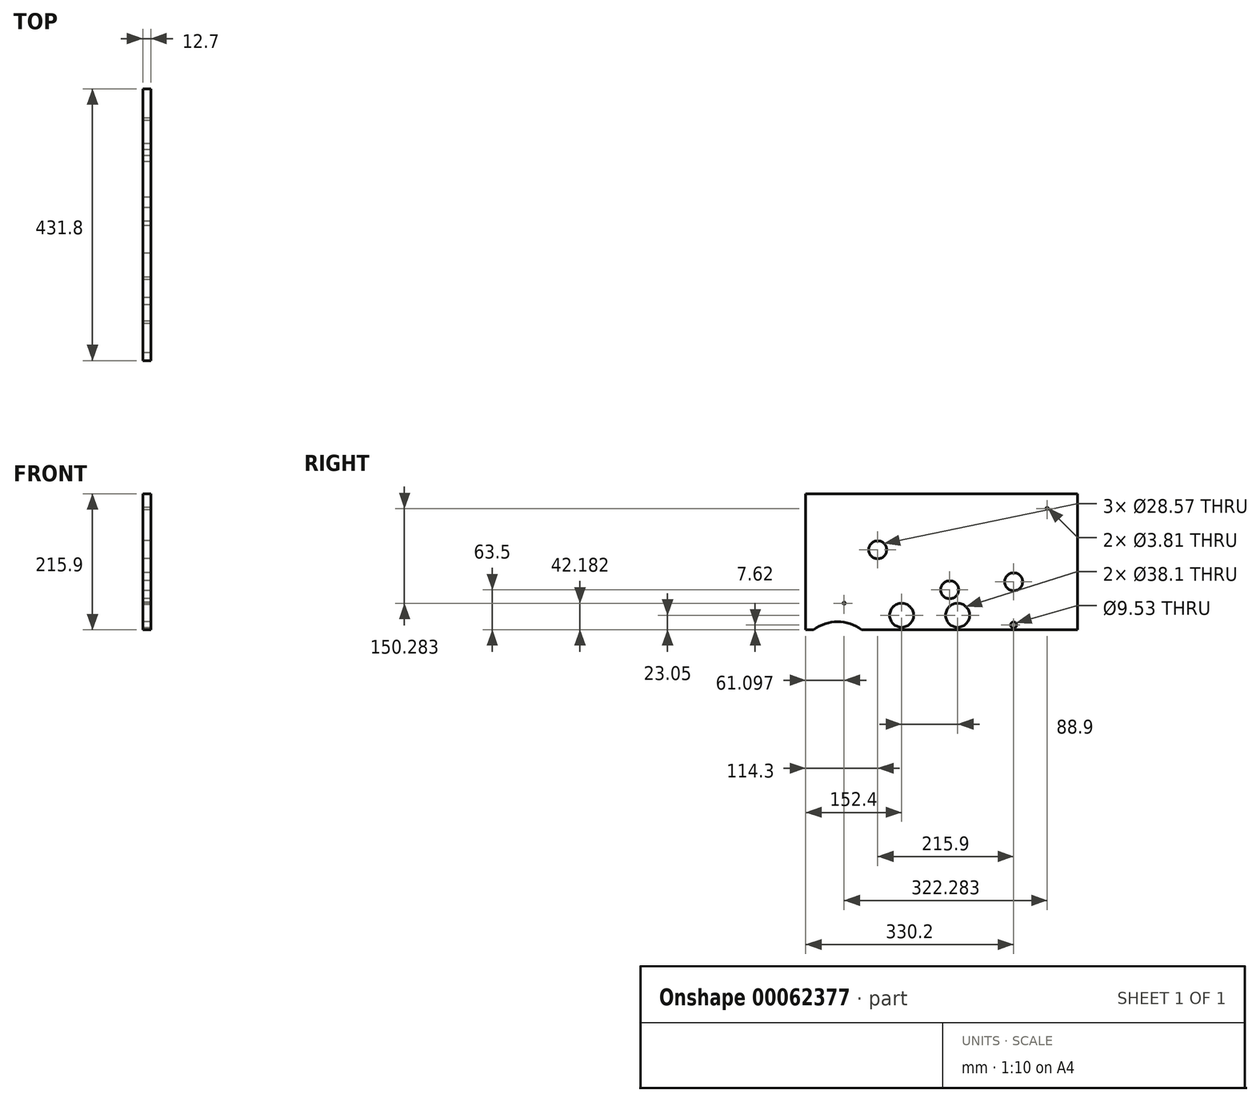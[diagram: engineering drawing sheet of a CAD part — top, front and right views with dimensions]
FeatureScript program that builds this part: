
annotation { "Feature Type Name" : "Feature", "Feature Type Description" : "" }
export const myFeature = defineFeature(function(context is Context, id is Id, definition is map)
    precondition{}
    {
        {
            var Q0;
            Q0=qCreatedBy(makeId("Right.planeOp"),FACE);
            var sketch = newSketch(context, id + "F0", { "sketchPlane" : qUnion([Q0])});
            skLineSegment(sketch, "E0.bottom", {"start": v(0, 0) * mm, "end": v(431.8, 0) * mm});
            skLineSegment(sketch, "E0.top", {"start": v(0, 355.6) * mm, "end": v(431.8, 355.6) * mm});
            skLineSegment(sketch, "E0.left", {"start": v(0, 0) * mm, "end": v(0, 355.6) * mm});
            skLineSegment(sketch, "E0.right", {"start": v(431.8, 0) * mm, "end": v(431.8, 355.6) * mm});
            skCircle(sketch, "E1", {"center": v(330.2, 7.62) * mm, "radius": 4.76 * mm});
            skCircle(sketch, "E2", {"center": v(228.6, 63.5) * mm, "radius": 14.29 * mm});
            skCircle(sketch, "E3", {"center": v(114.3, 127) * mm, "radius": 14.29 * mm});
            skCircle(sketch, "E4", {"center": v(330.2, 76.2) * mm, "radius": 14.29 * mm});
            skLineSegment(sketch, "E5", {"start": v(38.08, 31.45) * mm, "end": v(406.4, 203.2) * mm, "construction": true});
            skLineSegment(sketch, "E6", {"start": v(406.4, 203.2) * mm, "end": v(406.4, 31.45) * mm, "construction": true});
            skLineSegment(sketch, "E7", {"start": v(406.4, 31.45) * mm, "end": v(38.08, 31.45) * mm, "construction": true});
            skCircle(sketch, "E8", {"center": v(383.38, 192.47) * mm, "radius": 1.9 * mm});
            skCircle(sketch, "E9", {"center": v(61.1, 42.18) * mm, "radius": 1.9 * mm});
            skCircle(sketch, "E10", {"center": v(50.8, -50.8) * mm, "radius": 63.5 * mm});
            skSolve(sketch);
        }
        {
            var Q0;
            Q0=makeQuery(id+"F0.imprint","IMPRINT",FACE,{"disambiguationData":[TD([[makeQuery(id+"F0.imprint","IMPRINT",EDGE,{"derivedFrom":sQuery(id+"F0.wireOp",EDGE,"E0.top")}),-1.0]])]});
            extrude(context, id + "F1", {"entities" : qUnion([Q0]), "depth" : 12.7 * mm});
        }
        {
            var Q0;
            Q0=makeQuery(id+"F1.opExtrude","CAP_FACE",FACE,{"disambiguationData":[OSD([sQuery(id+"F0.wireOp",EDGE,"E0.bottom"),sQuery(id+"F0.wireOp",EDGE,"E0.top"),sQuery(id+"F0.wireOp",EDGE,"E0.left"),sQuery(id+"F0.wireOp",EDGE,"E0.right"),sQuery(id+"F0.wireOp",EDGE,"E1"),sQuery(id+"F0.wireOp",EDGE,"E2"),sQuery(id+"F0.wireOp",EDGE,"E3"),sQuery(id+"F0.wireOp",EDGE,"E4"),sQuery(id+"F0.wireOp",EDGE,"E8"),sQuery(id+"F0.wireOp",EDGE,"E9"),sQuery(id+"F0.wireOp",EDGE,"E10")])],"isStart":false});
            var sketch = newSketch(context, id + "F2", { "sketchPlane" : qUnion([Q0])});
            skCircle(sketch, "E11", {"center": v(152.4, 23.05) * mm, "radius": 19.05 * mm});
            skCircle(sketch, "E12", {"center": v(241.3, 23.05) * mm, "radius": 19.05 * mm});
            skSolve(sketch);
        }
        {
            var Q0;
            Q0=makeQuery(id+"F2.imprint","IMPRINT",FACE,{"disambiguationData":[TD([[makeQuery(id+"F2.imprint","IMPRINT",EDGE,{"derivedFrom":sQuery(id+"F2.wireOp",EDGE,"E11")}),1.0]])]});
            var Q1;
            Q1=makeQuery(id+"F2.imprint","IMPRINT",FACE,{"disambiguationData":[TD([[makeQuery(id+"F2.imprint","IMPRINT",EDGE,{"derivedFrom":sQuery(id+"F2.wireOp",EDGE,"E12")}),1.0]])]});
            extrude(context, id + "F3", {"entities" : qUnion([Q0, Q1]), "operationType" : NewBodyOperationType.REMOVE, "oppositeDirection" : true, "depth" : 25.4 * mm});
        }
        {
            var Q0;
            Q0=makeQuery(id+"F1.opExtrude","CAP_FACE",FACE,{"disambiguationData":[OSD([sQuery(id+"F0.wireOp",EDGE,"E0.bottom"),sQuery(id+"F0.wireOp",EDGE,"E0.top"),sQuery(id+"F0.wireOp",EDGE,"E0.left"),sQuery(id+"F0.wireOp",EDGE,"E0.right"),sQuery(id+"F0.wireOp",EDGE,"E1"),sQuery(id+"F0.wireOp",EDGE,"E2"),sQuery(id+"F0.wireOp",EDGE,"E3"),sQuery(id+"F0.wireOp",EDGE,"E4"),sQuery(id+"F0.wireOp",EDGE,"E8"),sQuery(id+"F0.wireOp",EDGE,"E9"),sQuery(id+"F0.wireOp",EDGE,"E10")])],"isStart":false});
            var sketch = newSketch(context, id + "F4", { "sketchPlane" : qUnion([Q0])});
            skLineSegment(sketch, "E13.bottom", {"start": v(0, 355.6) * mm, "end": v(431.8, 355.6) * mm});
            skLineSegment(sketch, "E13.top", {"start": v(0, 215.9) * mm, "end": v(431.8, 215.9) * mm});
            skLineSegment(sketch, "E13.left", {"start": v(0, 355.6) * mm, "end": v(0, 215.9) * mm});
            skLineSegment(sketch, "E13.right", {"start": v(431.8, 355.6) * mm, "end": v(431.8, 215.9) * mm});
            skSolve(sketch);
        }
        {
            var Q0;
            Q0=makeQuery(id+"F4.imprint","IMPRINT",FACE,{"disambiguationData":[TD([[makeQuery(id+"F4.imprint","IMPRINT",EDGE,{"derivedFrom":sQuery(id+"F4.wireOp",EDGE,"E13.bottom")}),-1.0]])]});
            extrude(context, id + "F5", {"entities" : qUnion([Q0]), "operationType" : NewBodyOperationType.REMOVE, "endBound" : BoundingType.UP_TO_NEXT, "oppositeDirection" : true, "depth" : 25.4 * mm});
        }
    });
